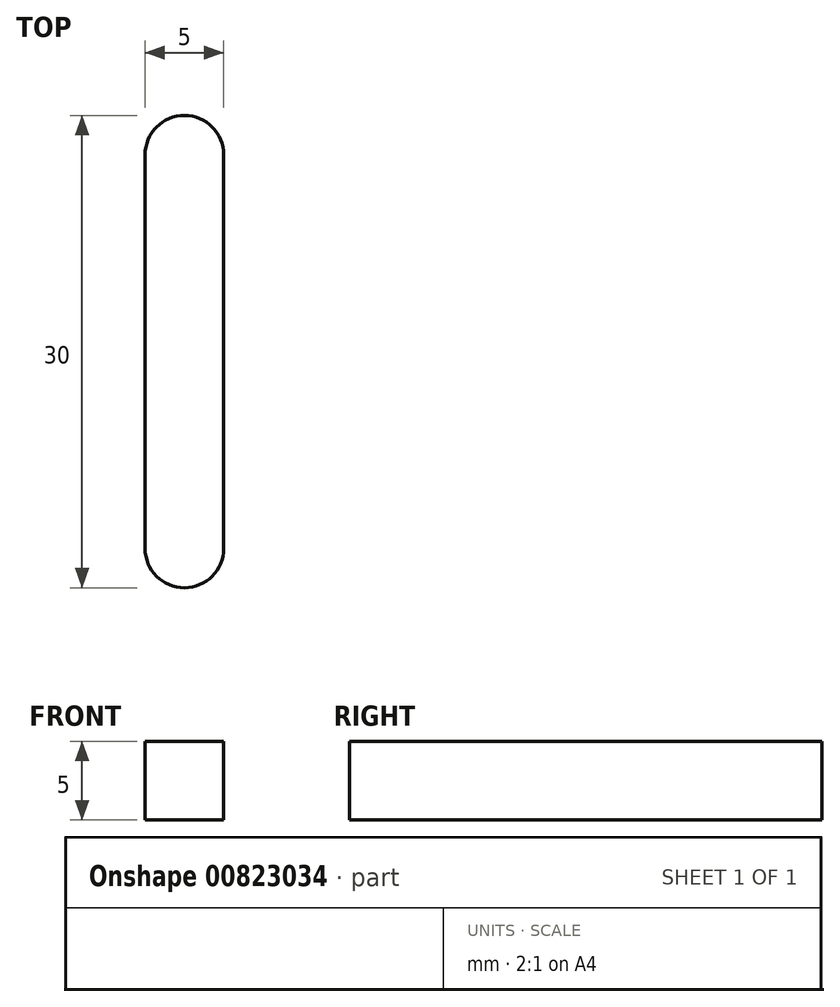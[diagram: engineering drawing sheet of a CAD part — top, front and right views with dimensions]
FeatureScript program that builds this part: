
annotation { "Feature Type Name" : "Feature", "Feature Type Description" : "" }
export const myFeature = defineFeature(function(context is Context, id is Id, definition is map)
    precondition{}
    {
        {
            var Q0;
            Q0=qCreatedBy(makeId("Top.planeOp"),FACE);
            var sketch = newSketch(context, id + "F0", { "sketchPlane" : qUnion([Q0])});
            skLineSegment(sketch, "E0.left", {"start": v(2.5, 12.5) * mm, "end": v(2.5, -12.5) * mm});
            skLineSegment(sketch, "E0.right", {"start": v(-2.5, 12.5) * mm, "end": v(-2.5, -12.5) * mm});
            skPoint(sketch, "E0.middle", {"position": v(0, 0) * mm});
            skArc(sketch, "E1", {"start": v(2.5, 12.5) * mm, "mid": v(0, 15) * mm, "end": v(-2.5, 12.5) * mm});
            skArc(sketch, "E2", {"start": v(-2.5, -12.5) * mm, "mid": v(0, -15) * mm, "end": v(2.5, -12.5) * mm});
            skSolve(sketch);
        }
        {
            var Q0;
            Q0=qSketchRegion(id+"F0",true);
            extrude(context, id + "F1", {"entities" : qUnion([Q0]), "depth" : 5 * mm, "offsetDistance" : 25 * mm});
        }
    });
